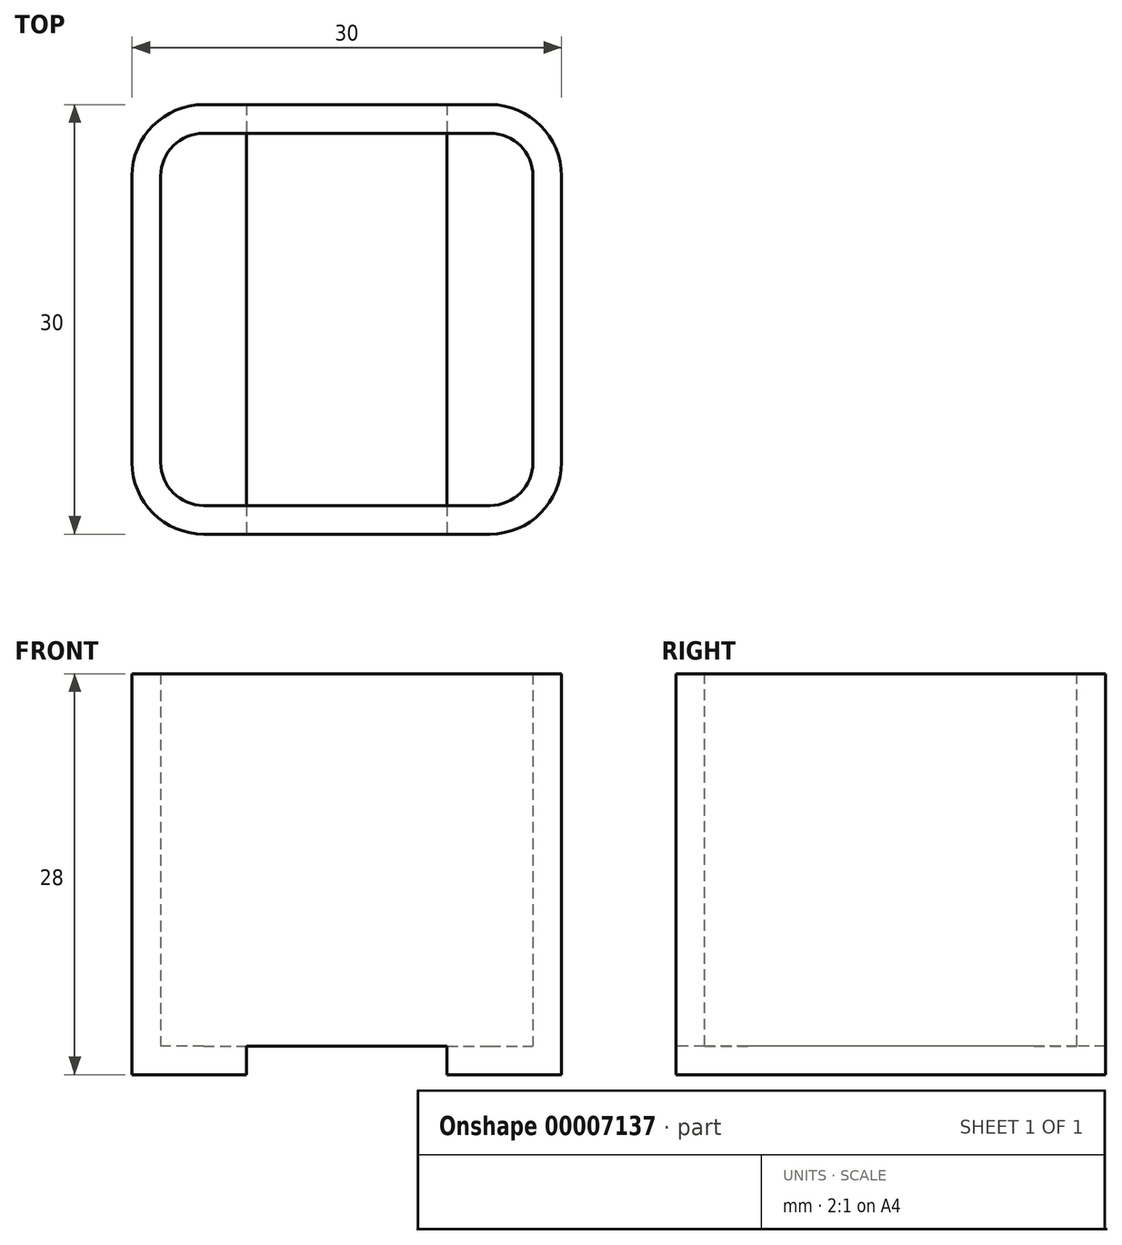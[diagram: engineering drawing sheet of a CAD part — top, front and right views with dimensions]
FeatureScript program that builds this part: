
annotation { "Feature Type Name" : "Feature", "Feature Type Description" : "" }
export const myFeature = defineFeature(function(context is Context, id is Id, definition is map)
    precondition{}
    {
        {
            var Q0;
            Q0=qCreatedBy(makeId("Top.planeOp"),FACE);
            var sketch = newSketch(context, id + "F0", { "sketchPlane" : qUnion([Q0])});
            skLineSegment(sketch, "E0.bottom", {"start": v(-13.13, 12.6) * mm, "end": v(16.87, 12.6) * mm});
            skLineSegment(sketch, "E0.top", {"start": v(-13.13, -17.4) * mm, "end": v(16.87, -17.4) * mm});
            skLineSegment(sketch, "E0.left", {"start": v(-13.13, 12.6) * mm, "end": v(-13.13, -17.4) * mm});
            skLineSegment(sketch, "E0.right", {"start": v(16.87, 12.6) * mm, "end": v(16.87, -17.4) * mm});
            skSolve(sketch);
        }
        {
            var Q0;
            Q0=makeQuery(id+"F0.imprint","IMPRINT",FACE,{"disambiguationData":[TD([[makeQuery(id+"F0.imprint","IMPRINT",EDGE,{"derivedFrom":sQuery(id+"F0.wireOp",EDGE,"E0.bottom")}),-1.0]])]});
            extrude(context, id + "F1", {"entities" : qUnion([Q0]), "depth" : 28 * mm});
        }
        {
            var Q0;
            Q0=makeQuery(id+"F1.opExtrude","SWEPT_EDGE",EDGE,{"disambiguationData":[OSD([sQuery(id+"F0.wireOp",EDGE,"E0.top"),sQuery(id+"F0.wireOp",EDGE,"E0.right")])]});
            var Q1;
            Q1=makeQuery(id+"F1.opExtrude","SWEPT_EDGE",EDGE,{"disambiguationData":[OSD([sQuery(id+"F0.wireOp",EDGE,"E0.bottom"),sQuery(id+"F0.wireOp",EDGE,"E0.right")])]});
            var Q2;
            Q2=makeQuery(id+"F1.opExtrude","SWEPT_EDGE",EDGE,{"disambiguationData":[OSD([sQuery(id+"F0.wireOp",EDGE,"E0.bottom"),sQuery(id+"F0.wireOp",EDGE,"E0.left")])]});
            var Q3;
            Q3=makeQuery(id+"F1.opExtrude","SWEPT_EDGE",EDGE,{"disambiguationData":[OSD([sQuery(id+"F0.wireOp",EDGE,"E0.top"),sQuery(id+"F0.wireOp",EDGE,"E0.left")])]});
            fillet(context, id + "F2", {"entities" : qUnion([Q0, Q1, Q2, Q3]), "radius" : 5 * mm, "tangentPropagation" : true, "allowEdgeOverflow" : false});
        }
        {
            var Q0;
            Q0=makeQuery(id+"F1.opExtrude","CAP_FACE",FACE,{"disambiguationData":[OSD([sQuery(id+"F0.wireOp",EDGE,"E0.bottom"),sQuery(id+"F0.wireOp",EDGE,"E0.top"),sQuery(id+"F0.wireOp",EDGE,"E0.left"),sQuery(id+"F0.wireOp",EDGE,"E0.right")])],"isStart":false});
            shell(context, id + "F3", {"entities" : qUnion([Q0]), "thickness" : 2 * mm});
        }
        {
            var Q0;
            Q0=makeQuery(id+"F1.opExtrude","CAP_FACE",FACE,{"disambiguationData":[OSD([sQuery(id+"F0.wireOp",EDGE,"E0.bottom"),sQuery(id+"F0.wireOp",EDGE,"E0.top"),sQuery(id+"F0.wireOp",EDGE,"E0.left"),sQuery(id+"F0.wireOp",EDGE,"E0.right")])],"isStart":true});
            var sketch = newSketch(context, id + "F4", { "sketchPlane" : qUnion([Q0])});
            skLineSegment(sketch, "E1", {"start": v(-13.13, 17.4) * mm, "end": v(-13.13, -12.6) * mm});
            skLineSegment(sketch, "E2", {"start": v(-13.13, -12.6) * mm, "end": v(-5.13, -12.6) * mm});
            skLineSegment(sketch, "E3", {"start": v(-5.13, -12.6) * mm, "end": v(-5.13, 17.4) * mm});
            skLineSegment(sketch, "E4", {"start": v(-5.13, 17.4) * mm, "end": v(-13.13, 17.4) * mm});
            skLineSegment(sketch, "E5", {"start": v(16.87, 17.4) * mm, "end": v(16.87, -12.6) * mm});
            skLineSegment(sketch, "E6", {"start": v(16.87, -12.6) * mm, "end": v(8.87, -12.6) * mm});
            skLineSegment(sketch, "E7", {"start": v(8.87, -12.6) * mm, "end": v(8.87, 17.4) * mm});
            skLineSegment(sketch, "E8", {"start": v(8.87, 17.4) * mm, "end": v(16.87, 17.4) * mm});
            skSolve(sketch);
        }
        {
            var Q0;
            {var subQ2=sQuery(id+"F4.wireOp",EDGE,"E3");Q0=makeQuery(id+"F4.imprint","IMPRINT",FACE,{"disambiguationData":[TD([[makeQuery(id+"F4.imprint","IMPRINT",EDGE,{"derivedFrom":subQ2}),-1.0]])]});}
            var Q1;
            Q1=makeQuery(id+"F3.opShell","OFFSET_FACE",FACE,{"disambiguationData":[OSD([sQuery(id+"F0.wireOp",EDGE,"E0.bottom"),sQuery(id+"F0.wireOp",EDGE,"E0.top"),sQuery(id+"F0.wireOp",EDGE,"E0.left"),sQuery(id+"F0.wireOp",EDGE,"E0.right")])]});
            extrude(context, id + "F5", {"entities" : qUnion([Q0]), "operationType" : NewBodyOperationType.REMOVE, "endBound" : BoundingType.UP_TO_SURFACE, "oppositeDirection" : true, "endBoundEntityFace" : qUnion([Q1]), "depth" : 25 * mm});
        }
    });
